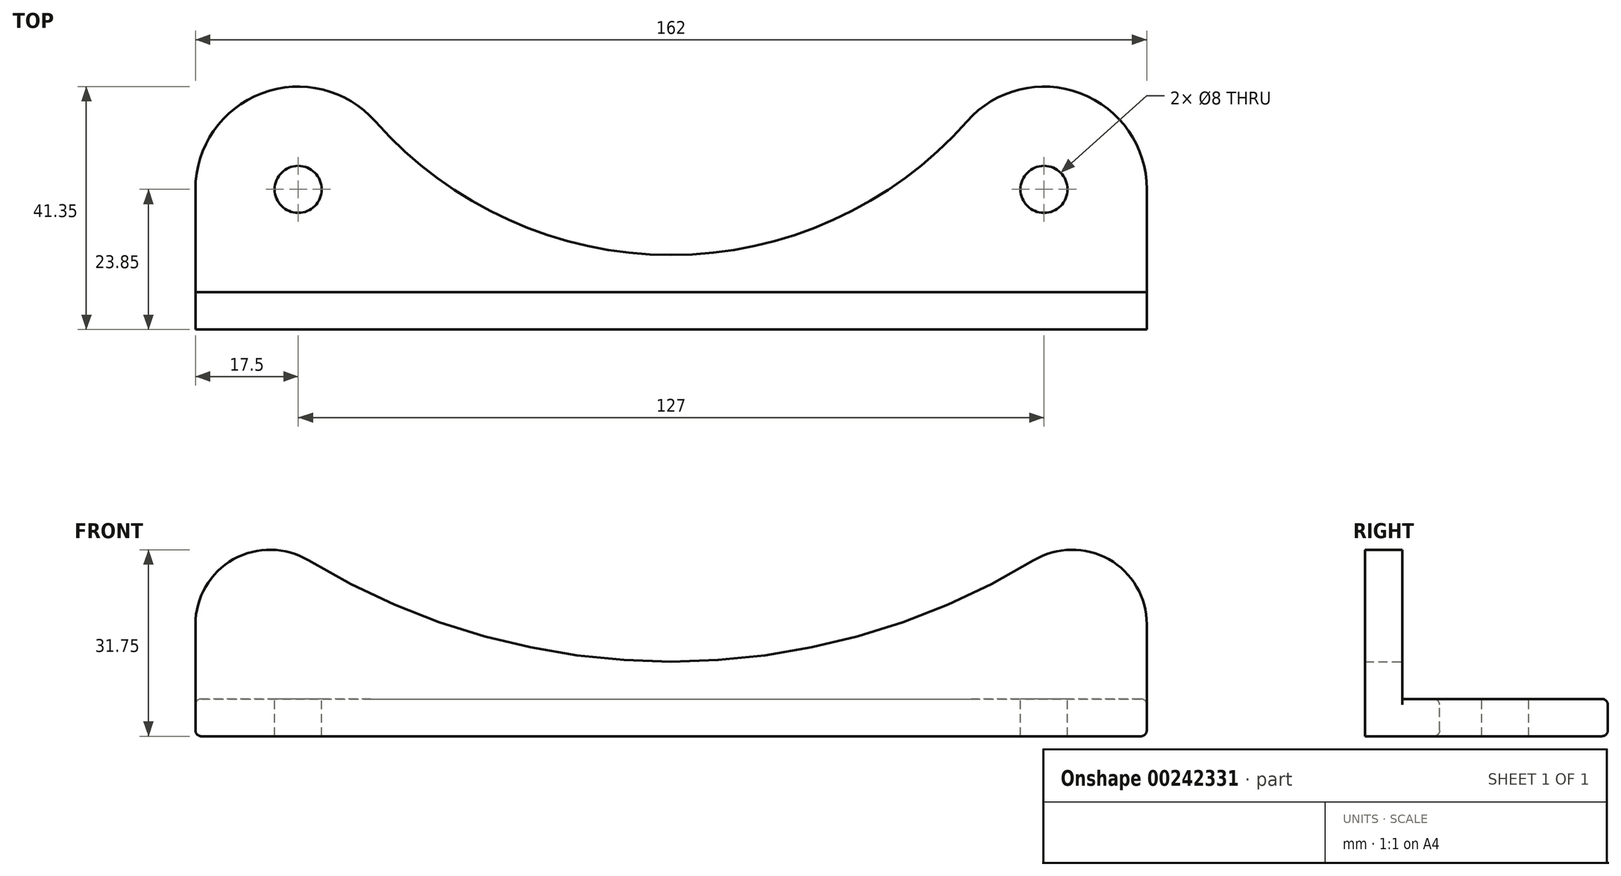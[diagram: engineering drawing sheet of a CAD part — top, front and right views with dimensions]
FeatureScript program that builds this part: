
annotation { "Feature Type Name" : "Feature", "Feature Type Description" : "" }
export const myFeature = defineFeature(function(context is Context, id is Id, definition is map)
    precondition{}
    {
        {
            var Q0;
            Q0=qCreatedBy(makeId("Top.planeOp"),FACE);
            var sketch = newSketch(context, id + "F0", { "sketchPlane" : qUnion([Q0])});
            skCircle(sketch, "E0", {"center": v(17.5, 17.5) * mm, "radius": 17.5 * mm});
            skCircle(sketch, "E1", {"center": v(144.5, 17.5) * mm, "radius": 17.5 * mm});
            skLineSegment(sketch, "E2", {"start": v(0, 0) * mm, "end": v(162, 0) * mm});
            skPoint(sketch, "E3.orphan", {"position": v(17.5, 0) * mm});
            skLineSegment(sketch, "E4", {"start": v(0, 0) * mm, "end": v(0, 17.5) * mm});
            skLineSegment(sketch, "E5", {"start": v(162, 0) * mm, "end": v(162, 17.5) * mm});
            skArc(sketch, "E6", {"start": v(30.62, 29.08) * mm, "mid": v(81, 6.35) * mm, "end": v(131.38, 29.08) * mm});
            skSolve(sketch);
        }
        {
            var Q0;
            {var subQ0=sQuery(id+"F0.wireOp",EDGE,"E0");var subQ1=makeQuery(id+"F0.imprint","INTERSECT",VERTEX,{"derivedFrom":[subQ0,sQuery(id+"F0.wireOp",EDGE,"E4")]});Q0=makeQuery(id+"F0.imprint","IMPRINT",FACE,{"disambiguationData":[TD([[makeQuery(id+"F0.imprint","IMPRINT",EDGE,{"disambiguationData":[TD([[subQ1,1.0]])],"derivedFrom":subQ0}),1.0]])]});}
            var Q1;
            {var subQ0=sQuery(id+"F0.wireOp",EDGE,"E4");Q1=makeQuery(id+"F0.imprint","IMPRINT",FACE,{"disambiguationData":[TD([[makeQuery(id+"F0.imprint","IMPRINT",EDGE,{"derivedFrom":subQ0}),-1.0]])]});}
            var Q2;
            {var subQ0=sQuery(id+"F0.wireOp",EDGE,"E6");Q2=makeQuery(id+"F0.imprint","IMPRINT",FACE,{"disambiguationData":[TD([[makeQuery(id+"F0.imprint","IMPRINT",EDGE,{"derivedFrom":subQ0}),-1.0]])]});}
            var Q3;
            {var subQ0=sQuery(id+"F0.wireOp",EDGE,"E1");var subQ1=makeQuery(id+"F0.imprint","INTERSECT",VERTEX,{"derivedFrom":[subQ0,sQuery(id+"F0.wireOp",EDGE,"E5")]});Q3=makeQuery(id+"F0.imprint","IMPRINT",FACE,{"disambiguationData":[TD([[makeQuery(id+"F0.imprint","IMPRINT",EDGE,{"disambiguationData":[TD([[subQ1,-1.0]])],"derivedFrom":subQ0}),1.0]])]});}
            var Q4;
            {var subQ0=sQuery(id+"F0.wireOp",EDGE,"E5");Q4=makeQuery(id+"F0.imprint","IMPRINT",FACE,{"disambiguationData":[TD([[makeQuery(id+"F0.imprint","IMPRINT",EDGE,{"derivedFrom":subQ0}),1.0]])]});}
            extrude(context, id + "F1", {"entities" : qUnion([Q0, Q1, Q2, Q3, Q4]), "oppositeDirection" : true, "depth" : 6.35 * mm});
        }
        {
            var Q0;
            Q0=makeQuery(id+"F1.opExtrude","CAP_FACE",FACE,{"disambiguationData":[OSD([sQuery(id+"F0.wireOp",EDGE,"E0"),sQuery(id+"F0.wireOp",EDGE,"E1"),sQuery(id+"F0.wireOp",EDGE,"E2"),sQuery(id+"F0.wireOp",EDGE,"E4"),sQuery(id+"F0.wireOp",EDGE,"E5"),sQuery(id+"F0.wireOp",EDGE,"E6")])],"isStart":false});
            var sketch = newSketch(context, id + "F2", { "sketchPlane" : qUnion([Q0])});
            skLineSegment(sketch, "E7.bottom", {"start": v(0, 0) * mm, "end": v(162, 0) * mm});
            skLineSegment(sketch, "E7.top", {"start": v(0, 6.35) * mm, "end": v(162, 6.35) * mm});
            skLineSegment(sketch, "E7.left", {"start": v(0, 0) * mm, "end": v(0, 6.35) * mm});
            skLineSegment(sketch, "E7.right", {"start": v(162, 0) * mm, "end": v(162, 6.35) * mm});
            skSolve(sketch);
        }
        {
            var Q0;
            Q0=makeQuery(id+"F2.imprint","IMPRINT",FACE,{"disambiguationData":[TD([[makeQuery(id+"F2.imprint","IMPRINT",EDGE,{"derivedFrom":sQuery(id+"F2.wireOp",EDGE,"E7.bottom")}),1.0]])]});
            extrude(context, id + "F3", {"entities" : qUnion([Q0]), "operationType" : NewBodyOperationType.ADD, "oppositeDirection" : true, "depth" : 35 * mm + 6.35 * mm});
        }
        {
            var Q0;
            Q0=makeQuery(id+"F1.opExtrude","CAP_FACE",FACE,{"disambiguationData":[OSD([sQuery(id+"F0.wireOp",EDGE,"E0"),sQuery(id+"F0.wireOp",EDGE,"E1"),sQuery(id+"F0.wireOp",EDGE,"E2"),sQuery(id+"F0.wireOp",EDGE,"E4"),sQuery(id+"F0.wireOp",EDGE,"E5"),sQuery(id+"F0.wireOp",EDGE,"E6")])],"isStart":true});
            var sketch = newSketch(context, id + "F4", { "sketchPlane" : qUnion([Q0])});
            skCircle(sketch, "E8", {"center": v(144.5, 17.5) * mm, "radius": 5.9 * mm});
            skCircle(sketch, "E9", {"center": v(17.5, 17.5) * mm, "radius": 7 * mm});
            skSolve(sketch);
        }
        {
            var Q0;
            Q0=sQuery(id+"F4.wireOp",VERTEX,"E9.center");
            var Q1;
            Q1=sQuery(id+"F4.wireOp",VERTEX,"E8.center");
            var Q2;
            Q2=makeQuery(id+"F1.opExtrude","SWEPT_BODY",BODY,{"disambiguationData":[OSD([sQuery(id+"F0.wireOp",EDGE,"E0"),sQuery(id+"F0.wireOp",EDGE,"E1"),sQuery(id+"F0.wireOp",EDGE,"E2"),sQuery(id+"F0.wireOp",EDGE,"E4"),sQuery(id+"F0.wireOp",EDGE,"E5"),sQuery(id+"F0.wireOp",EDGE,"E6")])]});
            hole(context, id + "F5", {"style" : HoleStyle.SIMPLE, "endStyle" : HoleEndStyle.THROUGH, "holeDiameter" : 8 * mm, "locations" : qUnion([Q0, Q1]), "scope" : qUnion([Q2]), "isTappedThrough" : true});
        }
        {
            var Q0;
            Q0=makeQuery(id+"F3.opExtrude","SWEPT_FACE",FACE,{"disambiguationData":[OSD([sQuery(id+"F2.wireOp",EDGE,"E7.bottom")])]});
            var sketch = newSketch(context, id + "F6", { "sketchPlane" : qUnion([Q0])});
            skCircle(sketch, "E10", {"center": v(-12.7, 12.7) * mm, "radius": 12.7 * mm});
            skCircle(sketch, "E11", {"center": v(-149.3, 12.7) * mm, "radius": 12.7 * mm});
            skLineSegment(sketch, "E12", {"start": v(0, 0) * mm, "end": v(0, 12.7) * mm});
            skLineSegment(sketch, "E13", {"start": v(-162, 0) * mm, "end": v(-162, 12.7) * mm});
            skArc(sketch, "E14", {"start": v(-142.73, 23.57) * mm, "mid": v(-81, 6.35) * mm, "end": v(-19.27, 23.57) * mm});
            skSolve(sketch);
        }
        {
            var Q0;
            {var subQ5=sQuery(id+"F6.wireOp",EDGE,"E14");Q0=makeQuery(id+"F6.imprint","IMPRINT",FACE,{"disambiguationData":[TD([[makeQuery(id+"F6.imprint","IMPRINT",EDGE,{"derivedFrom":subQ5}),1.0]])]});}
            extrude(context, id + "F7", {"entities" : qUnion([Q0]), "operationType" : NewBodyOperationType.REMOVE, "endBound" : BoundingType.UP_TO_NEXT, "oppositeDirection" : true, "depth" : 25.4 * mm});
        }
        {
            var Q0;
            Q0=makeQuery(id+"F1.opExtrude","CAP_EDGE",EDGE,{"disambiguationData":[OSD([sQuery(id+"F0.wireOp",EDGE,"E1")])],"isStart":true});
            var Q1;
            Q1=makeQuery(id+"F1.opExtrude","CAP_EDGE",EDGE,{"disambiguationData":[OSD([sQuery(id+"F0.wireOp",EDGE,"E2")])],"isStart":true});
            var Q2;
            Q2=makeQuery(id+"F1.opExtrude","CAP_EDGE",EDGE,{"disambiguationData":[OSD([sQuery(id+"F0.wireOp",EDGE,"E0")])],"isStart":false});
            var Q3;
            {var subQ0=sQuery(id+"F6.wireOp",EDGE,"E10");Q3=makeQuery(id+"F7.boolean.opBoolean","COPY",EDGE,{"derivedFrom":makeQuery(id+"F7.opExtrude","TWEAK_EDGE",EDGE,{"derivedFrom":[makeQuery(id+"F3.opExtrude","SWEPT_FACE",FACE,{"disambiguationData":[OSD([sQuery(id+"F2.wireOp",EDGE,"E7.top")])]}),makeQuery(id+"F6.imprint","IMPRINT",EDGE,{"disambiguationData":[TD([[makeQuery(id+"F6.imprint","INTERSECT",VERTEX,{"derivedFrom":[subQ0,sQuery(id+"F6.wireOp",EDGE,"E14")]}),1.0]])],"derivedFrom":subQ0})]})});}
            var Q4;
            Q4=makeQuery(id+"F5.hole-0.boolean.opBoolean","COPY",EDGE,{"derivedFrom":makeQuery(id+"F5.hole-0.opRevolve","SWEPT_EDGE",EDGE,{"disambiguationData":[OSD([sQuery(id+"F5.hole-0.sketch.wireOp",EDGE,"core_line_2"),sQuery(id+"F5.hole-0.sketch.wireOp",EDGE,"core_line_3")])]})});
            var Q5;
            Q5=makeQuery(id+"F5.hole-1.boolean.opBoolean","COPY",EDGE,{"derivedFrom":makeQuery(id+"F5.hole-1.opRevolve","SWEPT_EDGE",EDGE,{"disambiguationData":[OSD([sQuery(id+"F5.hole-1.sketch.wireOp",EDGE,"core_line_2"),sQuery(id+"F5.hole-1.sketch.wireOp",EDGE,"core_line_3")])]})});
            var Q6;
            Q6=makeQuery(id+"F5.hole-1.boolean.opBoolean","INTERSECT",EDGE,{"derivedFrom":[makeQuery(id+"F3.boolean.opBoolean","MERGE",FACE,{"derivedFrom":[makeQuery(id+"F1.opExtrude","CAP_FACE",FACE,{"disambiguationData":[OSD([sQuery(id+"F0.wireOp",EDGE,"E0"),sQuery(id+"F0.wireOp",EDGE,"E1"),sQuery(id+"F0.wireOp",EDGE,"E2"),sQuery(id+"F0.wireOp",EDGE,"E4"),sQuery(id+"F0.wireOp",EDGE,"E5"),sQuery(id+"F0.wireOp",EDGE,"E6")])],"isStart":false}),makeQuery(id+"F3.opExtrude","CAP_FACE",FACE,{"disambiguationData":[OSD([sQuery(id+"F2.wireOp",EDGE,"E7.bottom"),sQuery(id+"F2.wireOp",EDGE,"E7.top"),sQuery(id+"F2.wireOp",EDGE,"E7.left"),sQuery(id+"F2.wireOp",EDGE,"E7.right")])],"isStart":true})]}),makeQuery(id+"F5.hole-1.opRevolve","SWEPT_FACE",FACE,{"disambiguationData":[OSD([sQuery(id+"F5.hole-1.sketch.wireOp",EDGE,"core_line_2")])]})]});
            var Q7;
            Q7=makeQuery(id+"F5.hole-0.boolean.opBoolean","INTERSECT",EDGE,{"derivedFrom":[makeQuery(id+"F3.boolean.opBoolean","MERGE",FACE,{"derivedFrom":[makeQuery(id+"F1.opExtrude","CAP_FACE",FACE,{"disambiguationData":[OSD([sQuery(id+"F0.wireOp",EDGE,"E0"),sQuery(id+"F0.wireOp",EDGE,"E1"),sQuery(id+"F0.wireOp",EDGE,"E2"),sQuery(id+"F0.wireOp",EDGE,"E4"),sQuery(id+"F0.wireOp",EDGE,"E5"),sQuery(id+"F0.wireOp",EDGE,"E6")])],"isStart":false}),makeQuery(id+"F3.opExtrude","CAP_FACE",FACE,{"disambiguationData":[OSD([sQuery(id+"F2.wireOp",EDGE,"E7.bottom"),sQuery(id+"F2.wireOp",EDGE,"E7.top"),sQuery(id+"F2.wireOp",EDGE,"E7.left"),sQuery(id+"F2.wireOp",EDGE,"E7.right")])],"isStart":true})]}),makeQuery(id+"F5.hole-0.opRevolve","SWEPT_FACE",FACE,{"disambiguationData":[OSD([sQuery(id+"F5.hole-0.sketch.wireOp",EDGE,"core_line_2")])]})]});
            fillet(context, id + "F8", {"entities" : qUnion([Q0, Q1, Q2, Q3, Q4, Q5, Q6, Q7]), "radius" : 1 * mm, "tangentPropagation" : true, "allowEdgeOverflow" : false});
        }
    });
